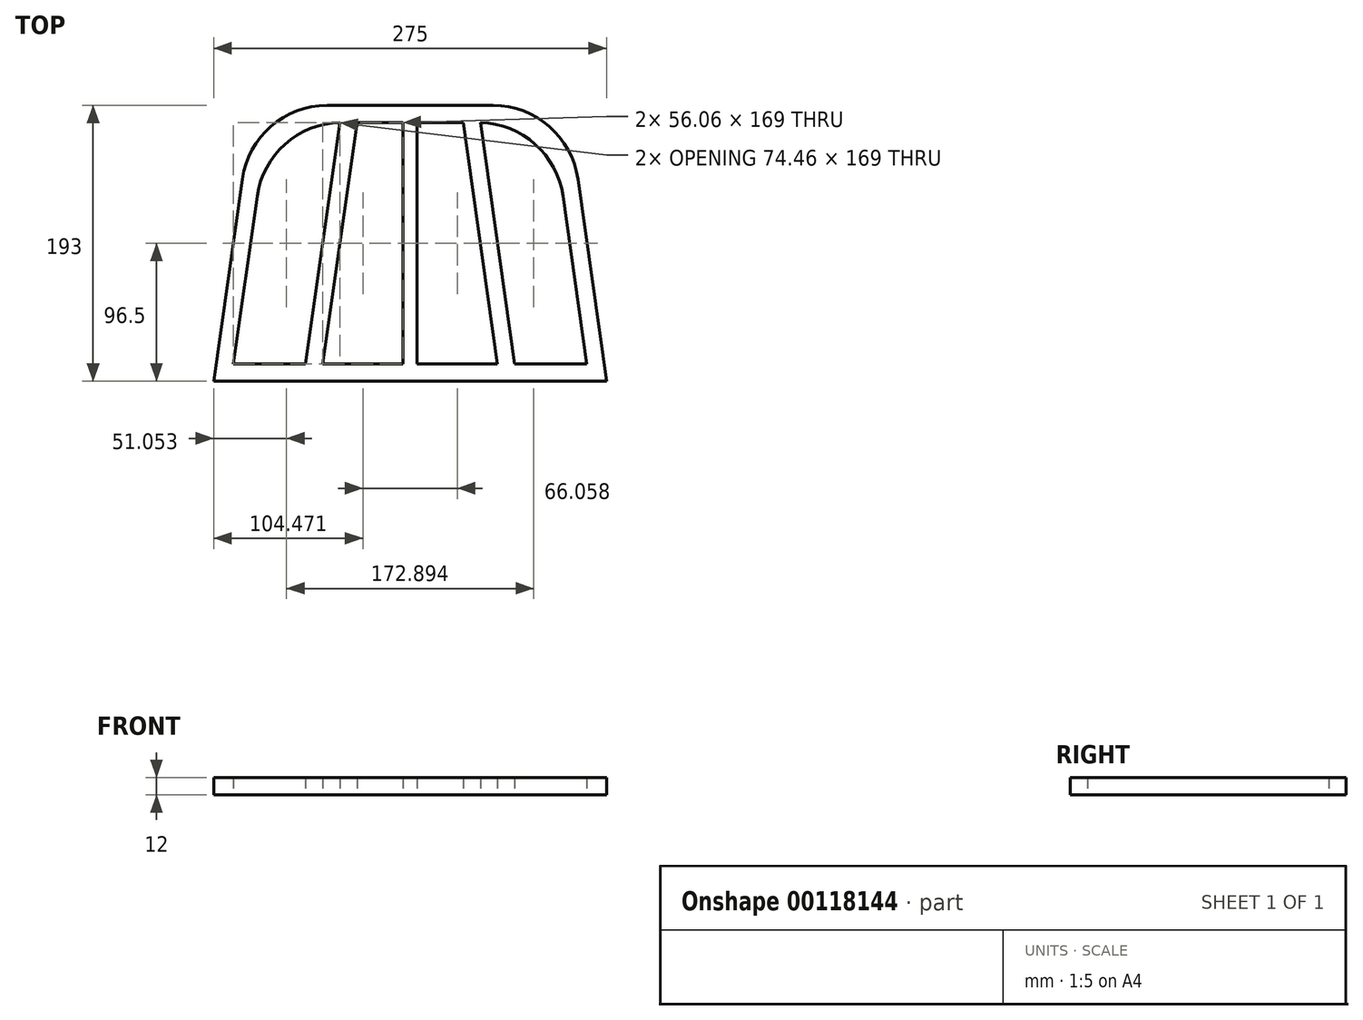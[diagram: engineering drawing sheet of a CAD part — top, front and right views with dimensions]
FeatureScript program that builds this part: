
annotation { "Feature Type Name" : "Feature", "Feature Type Description" : "" }
export const myFeature = defineFeature(function(context is Context, id is Id, definition is map)
    precondition{}
    {
        {
            var Q0;
            Q0=qCreatedBy(makeId("Top.planeOp"),FACE);
            var sketch = newSketch(context, id + "F0", { "sketchPlane" : qUnion([Q0])});
            skLineSegment(sketch, "E0", {"start": v(0, 0) * mm, "end": v(275, 0) * mm});
            skLineSegment(sketch, "E1.0", {"start": v(1.7, 12) * mm, "end": v(137.5, 12) * mm});
            skLineSegment(sketch, "E2.0", {"start": v(18.3, 129) * mm, "end": v(137.5, 129) * mm});
            skLineSegment(sketch, "E3.0", {"start": v(20, 141) * mm, "end": v(137.5, 141) * mm});
            skLineSegment(sketch, "E4.0", {"start": v(25.66, 181) * mm, "end": v(137.5, 181) * mm});
            skLineSegment(sketch, "E5.0", {"start": v(27.37, 193) * mm, "end": v(137.5, 193) * mm});
            skPoint(sketch, "E6", {"position": v(137.5, 0) * mm});
            skLineSegment(sketch, "E7", {"start": v(137.5, 0) * mm, "end": v(137.5, 214.03) * mm, "construction": true});
            skPoint(sketch, "E8", {"position": v(137.5, 67) * mm});
            skLineSegment(sketch, "E9", {"start": v(137.5, 67) * mm, "end": v(9.5, 67) * mm});
            skLineSegment(sketch, "E10.0", {"start": v(137.5, 79) * mm, "end": v(11.2, 79) * mm});
            skLineSegment(sketch, "E11", {"start": v(0, 0) * mm, "end": v(27.37, 193) * mm});
            skLineSegment(sketch, "E12.MirrorCS", {"start": v(275, 0) * mm, "end": v(247.63, 193) * mm});
            skLineSegment(sketch, "E13.MirrorCS", {"start": v(249.34, 181) * mm, "end": v(137.5, 181) * mm});
            skLineSegment(sketch, "E14.MirrorCS", {"start": v(247.63, 193) * mm, "end": v(137.5, 193) * mm});
            skLineSegment(sketch, "E15.MirrorCS", {"start": v(255, 141) * mm, "end": v(137.5, 141) * mm});
            skLineSegment(sketch, "E16.MirrorCS", {"start": v(256.7, 129) * mm, "end": v(137.5, 129) * mm});
            skLineSegment(sketch, "E17.MirrorCS", {"start": v(137.5, 79) * mm, "end": v(263.8, 79) * mm});
            skLineSegment(sketch, "E18.MirrorCS", {"start": v(137.5, 67) * mm, "end": v(265.5, 67) * mm});
            skLineSegment(sketch, "E19.0", {"start": v(12.12, 0) * mm, "end": v(39.49, 193) * mm});
            skLineSegment(sketch, "E20.MirrorCS", {"start": v(262.88, 0) * mm, "end": v(235.51, 193) * mm});
            skLineSegment(sketch, "E21.MirrorCS", {"start": v(273.3, 12) * mm, "end": v(137.5, 12) * mm});
            skLineSegment(sketch, "E22.0", {"start": v(142.5, 0) * mm, "end": v(142.5, 214.03) * mm});
            skLineSegment(sketch, "E23.0", {"start": v(212.38, 0) * mm, "end": v(185.01, 193) * mm});
            skLineSegment(sketch, "E24.0", {"start": v(200.26, 0) * mm, "end": v(172.9, 193) * mm});
            skLineSegment(sketch, "E25.MirrorCS", {"start": v(132.5, 0) * mm, "end": v(132.5, 214.03) * mm});
            skLineSegment(sketch, "E26.MirrorCS", {"start": v(74.74, 0) * mm, "end": v(102.1, 193) * mm});
            skLineSegment(sketch, "E27.MirrorCS", {"start": v(62.62, 0) * mm, "end": v(89.99, 193) * mm});
            skSolve(sketch);
        }
        {
            var Q0;
            {var subQ5=sQuery(id+"F0.wireOp",EDGE,"E13.MirrorCS");var subQ6=sQuery(id+"F0.wireOp",EDGE,"E4.0");var subQ7=makeQuery(id+"F0.imprint","INTERSECT",VERTEX,{"derivedFrom":[subQ6,subQ5]});Q0=makeQuery(id+"F0.imprint","IMPRINT",FACE,{"disambiguationData":[TD([[makeQuery(id+"F0.imprint","IMPRINT",EDGE,{"disambiguationData":[TD([[subQ7,1.0]])],"derivedFrom":subQ6}),1.0]])]});}
            var Q1;
            {var subQ0=sQuery(id+"F0.wireOp",EDGE,"E11");var subQ1=sQuery(id+"F0.wireOp",EDGE,"E4.0");var subQ2=makeQuery(id+"F0.imprint","INTERSECT",VERTEX,{"derivedFrom":[subQ1,subQ0]});Q1=makeQuery(id+"F0.imprint","IMPRINT",FACE,{"disambiguationData":[TD([[makeQuery(id+"F0.imprint","IMPRINT",EDGE,{"disambiguationData":[TD([[subQ2,-1.0]])],"derivedFrom":subQ1}),1.0]])]});}
            var Q2;
            {var subQ0=sQuery(id+"F0.wireOp",EDGE,"E11");var subQ1=sQuery(id+"F0.wireOp",EDGE,"E3.0");var subQ2=makeQuery(id+"F0.imprint","INTERSECT",VERTEX,{"derivedFrom":[subQ1,subQ0]});Q2=makeQuery(id+"F0.imprint","IMPRINT",FACE,{"disambiguationData":[TD([[makeQuery(id+"F0.imprint","IMPRINT",EDGE,{"disambiguationData":[TD([[subQ2,-1.0]])],"derivedFrom":subQ1}),1.0]])]});}
            var Q3;
            {var subQ0=sQuery(id+"F0.wireOp",EDGE,"E11");var subQ1=sQuery(id+"F0.wireOp",EDGE,"E2.0");var subQ2=makeQuery(id+"F0.imprint","INTERSECT",VERTEX,{"derivedFrom":[subQ1,subQ0]});Q3=makeQuery(id+"F0.imprint","IMPRINT",FACE,{"disambiguationData":[TD([[makeQuery(id+"F0.imprint","IMPRINT",EDGE,{"disambiguationData":[TD([[subQ2,-1.0]])],"derivedFrom":subQ1}),1.0]])]});}
            var Q4;
            {var subQ0=sQuery(id+"F0.wireOp",EDGE,"E13.MirrorCS");var subQ1=sQuery(id+"F0.wireOp",EDGE,"E12.MirrorCS");var subQ2=makeQuery(id+"F0.imprint","INTERSECT",VERTEX,{"derivedFrom":[subQ1,subQ0]});Q4=makeQuery(id+"F0.imprint","IMPRINT",FACE,{"disambiguationData":[TD([[makeQuery(id+"F0.imprint","IMPRINT",EDGE,{"disambiguationData":[TD([[subQ2,1.0]])],"derivedFrom":subQ1}),1.0]])]});}
            var Q5;
            {var subQ0=sQuery(id+"F0.wireOp",EDGE,"E14.MirrorCS");var subQ1=sQuery(id+"F0.wireOp",EDGE,"E12.MirrorCS");var subQ2=makeQuery(id+"F0.imprint","INTERSECT",VERTEX,{"derivedFrom":[subQ1,subQ0]});Q5=makeQuery(id+"F0.imprint","IMPRINT",FACE,{"disambiguationData":[TD([[makeQuery(id+"F0.imprint","IMPRINT",EDGE,{"disambiguationData":[TD([[subQ2,1.0]])],"derivedFrom":subQ1}),1.0]])]});}
            var Q6;
            {var subQ0=sQuery(id+"F0.wireOp",EDGE,"E15.MirrorCS");var subQ1=sQuery(id+"F0.wireOp",EDGE,"E12.MirrorCS");var subQ2=makeQuery(id+"F0.imprint","INTERSECT",VERTEX,{"derivedFrom":[subQ1,subQ0]});Q6=makeQuery(id+"F0.imprint","IMPRINT",FACE,{"disambiguationData":[TD([[makeQuery(id+"F0.imprint","IMPRINT",EDGE,{"disambiguationData":[TD([[subQ2,1.0]])],"derivedFrom":subQ1}),1.0]])]});}
            var Q7;
            {var subQ0=sQuery(id+"F0.wireOp",EDGE,"E16.MirrorCS");var subQ1=sQuery(id+"F0.wireOp",EDGE,"E12.MirrorCS");var subQ2=makeQuery(id+"F0.imprint","INTERSECT",VERTEX,{"derivedFrom":[subQ1,subQ0]});Q7=makeQuery(id+"F0.imprint","IMPRINT",FACE,{"disambiguationData":[TD([[makeQuery(id+"F0.imprint","IMPRINT",EDGE,{"disambiguationData":[TD([[subQ2,1.0]])],"derivedFrom":subQ1}),1.0]])]});}
            var Q8;
            {var subQ0=sQuery(id+"F0.wireOp",EDGE,"E17.MirrorCS");var subQ1=sQuery(id+"F0.wireOp",EDGE,"E12.MirrorCS");var subQ2=makeQuery(id+"F0.imprint","INTERSECT",VERTEX,{"derivedFrom":[subQ1,subQ0]});Q8=makeQuery(id+"F0.imprint","IMPRINT",FACE,{"disambiguationData":[TD([[makeQuery(id+"F0.imprint","IMPRINT",EDGE,{"disambiguationData":[TD([[subQ2,1.0]])],"derivedFrom":subQ1}),1.0]])]});}
            var Q9;
            {var subQ0=sQuery(id+"F0.wireOp",EDGE,"E18.MirrorCS");var subQ1=sQuery(id+"F0.wireOp",EDGE,"E9");var subQ2=makeQuery(id+"F0.imprint","INTERSECT",VERTEX,{"derivedFrom":[subQ1,subQ0]});Q9=makeQuery(id+"F0.imprint","IMPRINT",FACE,{"disambiguationData":[TD([[makeQuery(id+"F0.imprint","IMPRINT",EDGE,{"disambiguationData":[TD([[subQ2,-1.0]])],"derivedFrom":subQ1}),-1.0]])]});}
            var Q10;
            {var subQ0=sQuery(id+"F0.wireOp",EDGE,"E18.MirrorCS");var subQ1=sQuery(id+"F0.wireOp",EDGE,"E12.MirrorCS");var subQ2=makeQuery(id+"F0.imprint","INTERSECT",VERTEX,{"derivedFrom":[subQ1,subQ0]});Q10=makeQuery(id+"F0.imprint","IMPRINT",FACE,{"disambiguationData":[TD([[makeQuery(id+"F0.imprint","IMPRINT",EDGE,{"disambiguationData":[TD([[subQ2,1.0]])],"derivedFrom":subQ1}),1.0]])]});}
            var Q11;
            {var subQ0=sQuery(id+"F0.wireOp",EDGE,"E12.MirrorCS");var subQ1=sQuery(id+"F0.wireOp",EDGE,"E0");var subQ2=makeQuery(id+"F0.imprint","INTERSECT",VERTEX,{"derivedFrom":[subQ1,subQ0]});Q11=makeQuery(id+"F0.imprint","IMPRINT",FACE,{"disambiguationData":[TD([[makeQuery(id+"F0.imprint","IMPRINT",EDGE,{"disambiguationData":[TD([[subQ2,1.0]])],"derivedFrom":subQ1}),1.0]])]});}
            var Q12;
            {var subQ0=sQuery(id+"F0.wireOp",EDGE,"E19.0");var subQ1=sQuery(id+"F0.wireOp",EDGE,"E0");var subQ2=makeQuery(id+"F0.imprint","INTERSECT",VERTEX,{"derivedFrom":[subQ1,subQ0]});Q12=makeQuery(id+"F0.imprint","IMPRINT",FACE,{"disambiguationData":[TD([[makeQuery(id+"F0.imprint","IMPRINT",EDGE,{"disambiguationData":[TD([[subQ2,-1.0]])],"derivedFrom":subQ1}),1.0]])]});}
            var Q13;
            {var subQ0=sQuery(id+"F0.wireOp",EDGE,"E11");var subQ1=sQuery(id+"F0.wireOp",EDGE,"E0");var subQ2=makeQuery(id+"F0.imprint","INTERSECT",VERTEX,{"derivedFrom":[subQ1,subQ0]});Q13=makeQuery(id+"F0.imprint","IMPRINT",FACE,{"disambiguationData":[TD([[makeQuery(id+"F0.imprint","IMPRINT",EDGE,{"disambiguationData":[TD([[subQ2,-1.0]])],"derivedFrom":subQ1}),1.0]])]});}
            var Q14;
            {var subQ0=sQuery(id+"F0.wireOp",EDGE,"E11");var subQ1=sQuery(id+"F0.wireOp",EDGE,"E1.0");var subQ2=makeQuery(id+"F0.imprint","INTERSECT",VERTEX,{"derivedFrom":[subQ1,subQ0]});Q14=makeQuery(id+"F0.imprint","IMPRINT",FACE,{"disambiguationData":[TD([[makeQuery(id+"F0.imprint","IMPRINT",EDGE,{"disambiguationData":[TD([[subQ2,-1.0]])],"derivedFrom":subQ1}),1.0]])]});}
            var Q15;
            {var subQ0=sQuery(id+"F0.wireOp",EDGE,"E11");var subQ1=sQuery(id+"F0.wireOp",EDGE,"E9");var subQ2=makeQuery(id+"F0.imprint","INTERSECT",VERTEX,{"derivedFrom":[subQ1,subQ0]});Q15=makeQuery(id+"F0.imprint","IMPRINT",FACE,{"disambiguationData":[TD([[makeQuery(id+"F0.imprint","IMPRINT",EDGE,{"disambiguationData":[TD([[subQ2,1.0]])],"derivedFrom":subQ1}),-1.0]])]});}
            var Q16;
            {var subQ0=sQuery(id+"F0.wireOp",EDGE,"E11");var subQ1=sQuery(id+"F0.wireOp",EDGE,"E2.0");var subQ2=makeQuery(id+"F0.imprint","INTERSECT",VERTEX,{"derivedFrom":[subQ1,subQ0]});Q16=makeQuery(id+"F0.imprint","IMPRINT",FACE,{"disambiguationData":[TD([[makeQuery(id+"F0.imprint","IMPRINT",EDGE,{"disambiguationData":[TD([[subQ2,-1.0]])],"derivedFrom":subQ1}),-1.0]])]});}
            var Q17;
            {var subQ0=sQuery(id+"F0.wireOp",EDGE,"E16.MirrorCS");var subQ1=sQuery(id+"F0.wireOp",EDGE,"E2.0");var subQ2=makeQuery(id+"F0.imprint","INTERSECT",VERTEX,{"derivedFrom":[subQ1,subQ0]});Q17=makeQuery(id+"F0.imprint","IMPRINT",FACE,{"disambiguationData":[TD([[makeQuery(id+"F0.imprint","IMPRINT",EDGE,{"disambiguationData":[TD([[subQ2,1.0]])],"derivedFrom":subQ1}),1.0]])]});}
            var Q18;
            {var subQ0=sQuery(id+"F0.wireOp",EDGE,"E27.MirrorCS");var subQ1=sQuery(id+"F0.wireOp",EDGE,"E1.0");var subQ2=makeQuery(id+"F0.imprint","INTERSECT",VERTEX,{"derivedFrom":[subQ1,subQ0]});Q18=makeQuery(id+"F0.imprint","IMPRINT",FACE,{"disambiguationData":[TD([[makeQuery(id+"F0.imprint","IMPRINT",EDGE,{"disambiguationData":[TD([[subQ2,-1.0]])],"derivedFrom":subQ1}),1.0]])]});}
            var Q19;
            {var subQ0=sQuery(id+"F0.wireOp",EDGE,"E27.MirrorCS");var subQ1=sQuery(id+"F0.wireOp",EDGE,"E2.0");var subQ2=makeQuery(id+"F0.imprint","INTERSECT",VERTEX,{"derivedFrom":[subQ1,subQ0]});Q19=makeQuery(id+"F0.imprint","IMPRINT",FACE,{"disambiguationData":[TD([[makeQuery(id+"F0.imprint","IMPRINT",EDGE,{"disambiguationData":[TD([[subQ2,-1.0]])],"derivedFrom":subQ1}),-1.0]])]});}
            var Q20;
            {var subQ0=sQuery(id+"F0.wireOp",EDGE,"E27.MirrorCS");var subQ1=sQuery(id+"F0.wireOp",EDGE,"E3.0");var subQ2=makeQuery(id+"F0.imprint","INTERSECT",VERTEX,{"derivedFrom":[subQ1,subQ0]});Q20=makeQuery(id+"F0.imprint","IMPRINT",FACE,{"disambiguationData":[TD([[makeQuery(id+"F0.imprint","IMPRINT",EDGE,{"disambiguationData":[TD([[subQ2,-1.0]])],"derivedFrom":subQ1}),1.0]])]});}
            var Q21;
            {var subQ0=sQuery(id+"F0.wireOp",EDGE,"E19.0");var subQ1=sQuery(id+"F0.wireOp",EDGE,"E4.0");var subQ2=makeQuery(id+"F0.imprint","INTERSECT",VERTEX,{"derivedFrom":[subQ1,subQ0]});Q21=makeQuery(id+"F0.imprint","IMPRINT",FACE,{"disambiguationData":[TD([[makeQuery(id+"F0.imprint","IMPRINT",EDGE,{"disambiguationData":[TD([[subQ2,-1.0]])],"derivedFrom":subQ1}),1.0]])]});}
            var Q22;
            {var subQ0=sQuery(id+"F0.wireOp",EDGE,"E26.MirrorCS");var subQ1=sQuery(id+"F0.wireOp",EDGE,"E4.0");var subQ2=makeQuery(id+"F0.imprint","INTERSECT",VERTEX,{"derivedFrom":[subQ1,subQ0]});Q22=makeQuery(id+"F0.imprint","IMPRINT",FACE,{"disambiguationData":[TD([[makeQuery(id+"F0.imprint","IMPRINT",EDGE,{"disambiguationData":[TD([[subQ2,-1.0]])],"derivedFrom":subQ1}),1.0]])]});}
            var Q23;
            {var subQ0=sQuery(id+"F0.wireOp",EDGE,"E24.0");var subQ1=sQuery(id+"F0.wireOp",EDGE,"E13.MirrorCS");var subQ2=makeQuery(id+"F0.imprint","INTERSECT",VERTEX,{"derivedFrom":[subQ1,subQ0]});Q23=makeQuery(id+"F0.imprint","IMPRINT",FACE,{"disambiguationData":[TD([[makeQuery(id+"F0.imprint","IMPRINT",EDGE,{"disambiguationData":[TD([[subQ2,-1.0]])],"derivedFrom":subQ1}),-1.0]])]});}
            var Q24;
            {var subQ0=sQuery(id+"F0.wireOp",EDGE,"E20.MirrorCS");var subQ1=sQuery(id+"F0.wireOp",EDGE,"E13.MirrorCS");var subQ2=makeQuery(id+"F0.imprint","INTERSECT",VERTEX,{"derivedFrom":[subQ1,subQ0]});Q24=makeQuery(id+"F0.imprint","IMPRINT",FACE,{"disambiguationData":[TD([[makeQuery(id+"F0.imprint","IMPRINT",EDGE,{"disambiguationData":[TD([[subQ2,-1.0]])],"derivedFrom":subQ1}),-1.0]])]});}
            var Q25;
            {var subQ0=sQuery(id+"F0.wireOp",EDGE,"E23.0");var subQ1=sQuery(id+"F0.wireOp",EDGE,"E13.MirrorCS");var subQ2=makeQuery(id+"F0.imprint","INTERSECT",VERTEX,{"derivedFrom":[subQ1,subQ0]});Q25=makeQuery(id+"F0.imprint","IMPRINT",FACE,{"disambiguationData":[TD([[makeQuery(id+"F0.imprint","IMPRINT",EDGE,{"disambiguationData":[TD([[subQ2,-1.0]])],"derivedFrom":subQ1}),-1.0]])]});}
            var Q26;
            {var subQ0=sQuery(id+"F0.wireOp",EDGE,"E23.0");var subQ1=sQuery(id+"F0.wireOp",EDGE,"E13.MirrorCS");var subQ2=makeQuery(id+"F0.imprint","INTERSECT",VERTEX,{"derivedFrom":[subQ1,subQ0]});Q26=makeQuery(id+"F0.imprint","IMPRINT",FACE,{"disambiguationData":[TD([[makeQuery(id+"F0.imprint","IMPRINT",EDGE,{"disambiguationData":[TD([[subQ2,-1.0]])],"derivedFrom":subQ1}),1.0]])]});}
            var Q27;
            {var subQ0=sQuery(id+"F0.wireOp",EDGE,"E23.0");var subQ1=sQuery(id+"F0.wireOp",EDGE,"E15.MirrorCS");var subQ2=makeQuery(id+"F0.imprint","INTERSECT",VERTEX,{"derivedFrom":[subQ1,subQ0]});Q27=makeQuery(id+"F0.imprint","IMPRINT",FACE,{"disambiguationData":[TD([[makeQuery(id+"F0.imprint","IMPRINT",EDGE,{"disambiguationData":[TD([[subQ2,-1.0]])],"derivedFrom":subQ1}),1.0]])]});}
            var Q28;
            {var subQ0=sQuery(id+"F0.wireOp",EDGE,"E23.0");var subQ1=sQuery(id+"F0.wireOp",EDGE,"E16.MirrorCS");var subQ2=makeQuery(id+"F0.imprint","INTERSECT",VERTEX,{"derivedFrom":[subQ1,subQ0]});Q28=makeQuery(id+"F0.imprint","IMPRINT",FACE,{"disambiguationData":[TD([[makeQuery(id+"F0.imprint","IMPRINT",EDGE,{"disambiguationData":[TD([[subQ2,-1.0]])],"derivedFrom":subQ1}),1.0]])]});}
            var Q29;
            {var subQ0=sQuery(id+"F0.wireOp",EDGE,"E24.0");var subQ1=sQuery(id+"F0.wireOp",EDGE,"E17.MirrorCS");var subQ2=makeQuery(id+"F0.imprint","INTERSECT",VERTEX,{"derivedFrom":[subQ1,subQ0]});Q29=makeQuery(id+"F0.imprint","IMPRINT",FACE,{"disambiguationData":[TD([[makeQuery(id+"F0.imprint","IMPRINT",EDGE,{"disambiguationData":[TD([[subQ2,-1.0]])],"derivedFrom":subQ1}),-1.0]])]});}
            var Q30;
            {var subQ0=sQuery(id+"F0.wireOp",EDGE,"E24.0");var subQ1=sQuery(id+"F0.wireOp",EDGE,"E18.MirrorCS");var subQ2=makeQuery(id+"F0.imprint","INTERSECT",VERTEX,{"derivedFrom":[subQ1,subQ0]});Q30=makeQuery(id+"F0.imprint","IMPRINT",FACE,{"disambiguationData":[TD([[makeQuery(id+"F0.imprint","IMPRINT",EDGE,{"disambiguationData":[TD([[subQ2,-1.0]])],"derivedFrom":subQ1}),-1.0]])]});}
            var Q31;
            {var subQ0=sQuery(id+"F0.wireOp",EDGE,"E20.MirrorCS");var subQ1=sQuery(id+"F0.wireOp",EDGE,"E0");var subQ2=makeQuery(id+"F0.imprint","INTERSECT",VERTEX,{"derivedFrom":[subQ1,subQ0]});Q31=makeQuery(id+"F0.imprint","IMPRINT",FACE,{"disambiguationData":[TD([[makeQuery(id+"F0.imprint","IMPRINT",EDGE,{"disambiguationData":[TD([[subQ2,1.0]])],"derivedFrom":subQ1}),1.0]])]});}
            var Q32;
            {var subQ0=sQuery(id+"F0.wireOp",EDGE,"E23.0");var subQ1=sQuery(id+"F0.wireOp",EDGE,"E0");var subQ2=makeQuery(id+"F0.imprint","INTERSECT",VERTEX,{"derivedFrom":[subQ1,subQ0]});Q32=makeQuery(id+"F0.imprint","IMPRINT",FACE,{"disambiguationData":[TD([[makeQuery(id+"F0.imprint","IMPRINT",EDGE,{"disambiguationData":[TD([[subQ2,1.0]])],"derivedFrom":subQ1}),1.0]])]});}
            var Q33;
            {var subQ0=sQuery(id+"F0.wireOp",EDGE,"E22.0");var subQ1=sQuery(id+"F0.wireOp",EDGE,"E0");var subQ2=makeQuery(id+"F0.imprint","INTERSECT",VERTEX,{"derivedFrom":[subQ1,subQ0]});Q33=makeQuery(id+"F0.imprint","IMPRINT",FACE,{"disambiguationData":[TD([[makeQuery(id+"F0.imprint","IMPRINT",EDGE,{"disambiguationData":[TD([[subQ2,-1.0]])],"derivedFrom":subQ1}),1.0]])]});}
            var Q34;
            {var subQ0=sQuery(id+"F0.wireOp",EDGE,"E22.0");var subQ1=sQuery(id+"F0.wireOp",EDGE,"E0");var subQ2=makeQuery(id+"F0.imprint","INTERSECT",VERTEX,{"derivedFrom":[subQ1,subQ0]});Q34=makeQuery(id+"F0.imprint","IMPRINT",FACE,{"disambiguationData":[TD([[makeQuery(id+"F0.imprint","IMPRINT",EDGE,{"disambiguationData":[TD([[subQ2,1.0]])],"derivedFrom":subQ1}),1.0]])]});}
            var Q35;
            {var subQ0=sQuery(id+"F0.wireOp",EDGE,"E25.MirrorCS");var subQ1=sQuery(id+"F0.wireOp",EDGE,"E0");var subQ2=makeQuery(id+"F0.imprint","INTERSECT",VERTEX,{"derivedFrom":[subQ1,subQ0]});Q35=makeQuery(id+"F0.imprint","IMPRINT",FACE,{"disambiguationData":[TD([[makeQuery(id+"F0.imprint","IMPRINT",EDGE,{"disambiguationData":[TD([[subQ2,1.0]])],"derivedFrom":subQ1}),1.0]])]});}
            var Q36;
            {var subQ0=sQuery(id+"F0.wireOp",EDGE,"E26.MirrorCS");var subQ1=sQuery(id+"F0.wireOp",EDGE,"E0");var subQ2=makeQuery(id+"F0.imprint","INTERSECT",VERTEX,{"derivedFrom":[subQ1,subQ0]});Q36=makeQuery(id+"F0.imprint","IMPRINT",FACE,{"disambiguationData":[TD([[makeQuery(id+"F0.imprint","IMPRINT",EDGE,{"disambiguationData":[TD([[subQ2,1.0]])],"derivedFrom":subQ1}),1.0]])]});}
            var Q37;
            {var subQ0=sQuery(id+"F0.wireOp",EDGE,"E21.MirrorCS");var subQ1=sQuery(id+"F0.wireOp",EDGE,"E1.0");var subQ2=makeQuery(id+"F0.imprint","INTERSECT",VERTEX,{"derivedFrom":[subQ1,subQ0]});Q37=makeQuery(id+"F0.imprint","IMPRINT",FACE,{"disambiguationData":[TD([[makeQuery(id+"F0.imprint","IMPRINT",EDGE,{"disambiguationData":[TD([[subQ2,1.0]])],"derivedFrom":subQ1}),1.0]])]});}
            var Q38;
            {var subQ5=sQuery(id+"F0.wireOp",EDGE,"E16.MirrorCS");var subQ6=sQuery(id+"F0.wireOp",EDGE,"E2.0");var subQ7=makeQuery(id+"F0.imprint","INTERSECT",VERTEX,{"derivedFrom":[subQ6,subQ5]});Q38=makeQuery(id+"F0.imprint","IMPRINT",FACE,{"disambiguationData":[TD([[makeQuery(id+"F0.imprint","IMPRINT",EDGE,{"disambiguationData":[TD([[subQ7,1.0]])],"derivedFrom":subQ6}),-1.0]])]});}
            var Q39;
            {var subQ5=sQuery(id+"F0.wireOp",EDGE,"E15.MirrorCS");var subQ6=sQuery(id+"F0.wireOp",EDGE,"E3.0");var subQ7=makeQuery(id+"F0.imprint","INTERSECT",VERTEX,{"derivedFrom":[subQ6,subQ5]});Q39=makeQuery(id+"F0.imprint","IMPRINT",FACE,{"disambiguationData":[TD([[makeQuery(id+"F0.imprint","IMPRINT",EDGE,{"disambiguationData":[TD([[subQ7,1.0]])],"derivedFrom":subQ6}),1.0]])]});}
            var Q40;
            {var subQ0=sQuery(id+"F0.wireOp",EDGE,"E27.MirrorCS");var subQ1=sQuery(id+"F0.wireOp",EDGE,"E4.0");var subQ2=makeQuery(id+"F0.imprint","INTERSECT",VERTEX,{"derivedFrom":[subQ1,subQ0]});Q40=makeQuery(id+"F0.imprint","IMPRINT",FACE,{"disambiguationData":[TD([[makeQuery(id+"F0.imprint","IMPRINT",EDGE,{"disambiguationData":[TD([[subQ2,-1.0]])],"derivedFrom":subQ1}),1.0]])]});}
            var Q41;
            {var subQ0=sQuery(id+"F0.wireOp",EDGE,"E27.MirrorCS");var subQ1=sQuery(id+"F0.wireOp",EDGE,"E2.0");var subQ2=makeQuery(id+"F0.imprint","INTERSECT",VERTEX,{"derivedFrom":[subQ1,subQ0]});Q41=makeQuery(id+"F0.imprint","IMPRINT",FACE,{"disambiguationData":[TD([[makeQuery(id+"F0.imprint","IMPRINT",EDGE,{"disambiguationData":[TD([[subQ2,-1.0]])],"derivedFrom":subQ1}),1.0]])]});}
            var Q42;
            {var subQ0=sQuery(id+"F0.wireOp",EDGE,"E26.MirrorCS");var subQ1=sQuery(id+"F0.wireOp",EDGE,"E9");var subQ2=makeQuery(id+"F0.imprint","INTERSECT",VERTEX,{"derivedFrom":[subQ1,subQ0]});Q42=makeQuery(id+"F0.imprint","IMPRINT",FACE,{"disambiguationData":[TD([[makeQuery(id+"F0.imprint","IMPRINT",EDGE,{"disambiguationData":[TD([[subQ2,-1.0]])],"derivedFrom":subQ1}),-1.0]])]});}
            extrude(context, id + "F1", {"entities" : qUnion([Q0, Q1, Q2, Q3, Q4, Q5, Q6, Q7, Q8, Q9, Q10, Q11, Q12, Q13, Q14, Q15, Q16, Q17, Q18, Q19, Q20, Q21, Q22, Q23, Q24, Q25, Q26, Q27, Q28, Q29, Q30, Q31, Q32, Q33, Q34, Q35, Q36, Q37, Q38, Q39, Q40, Q41, Q42]), "depth" : 12 * mm});
        }
        {
            var Q0;
            Q0=makeQuery(id+"F1.opExtrude","SWEPT_EDGE",EDGE,{"disambiguationData":[OSD([sQuery(id+"F0.wireOp",EDGE,"E13.MirrorCS"),sQuery(id+"F0.wireOp",EDGE,"E20.MirrorCS")])]});
            var Q1;
            Q1=makeQuery(id+"F1.opExtrude","SWEPT_EDGE",EDGE,{"disambiguationData":[OSD([sQuery(id+"F0.wireOp",EDGE,"E4.0"),sQuery(id+"F0.wireOp",EDGE,"E19.0")])]});
            fillet(context, id + "F2", {"entities" : qUnion([Q0, Q1]), "radius" : 60 * mm, "tangentPropagation" : true, "allowEdgeOverflow" : false});
        }
        {
            var Q0;
            Q0=makeQuery(id+"F1.opExtrude","SWEPT_EDGE",EDGE,{"disambiguationData":[OSD([sQuery(id+"F0.wireOp",EDGE,"E5.0"),sQuery(id+"F0.wireOp",EDGE,"E11")])]});
            var Q1;
            Q1=makeQuery(id+"F1.opExtrude","SWEPT_EDGE",EDGE,{"disambiguationData":[OSD([sQuery(id+"F0.wireOp",EDGE,"E12.MirrorCS"),sQuery(id+"F0.wireOp",EDGE,"E14.MirrorCS")])]});
            fillet(context, id + "F3", {"entities" : qUnion([Q0, Q1]), "radius" : 60 * mm, "tangentPropagation" : true, "allowEdgeOverflow" : false});
        }
    });
